# Revit family: 252500.06 OSID Sender høy effekt Vegg
name_source: partatom
category: Fire Alarm Devices
revit_build: Autodesk Revit 2016 (Build: 20160314_0715(x64)
units: mm (PartAtom-declared; Revit-internal decimal feet)

## family parameters
Always vertical = Yes
Cut with Voids When Loaded = No
Maintain Annotation Orientation = No
OmniClass Number = 23.85.30.21.11.11.11
OmniClass Title = Smoke Detectors
Part Type = Normal
Room Calculation Point = No
Round Connector Dimension = Use Diameter
Shared = No
Work Plane-Based = No

## types (1)
- Linjedetektor sender
    Assembly Code = 5423
    CQ 2D Synlig = Yes
    CQ 3D Synlig = No
    CQ Coverage Circle = No
    CQ Coverage Circle Radius = 70000 mm  [stored 229.659 ft]
    CQ Height = 94 mm  [stored 0.308399 ft]
    CQ Høyre = No
    CQ Length = 198 mm  [stored 0.649606 ft]
    CQ Material = <By Category>
    CQ Type = LD
    CQ Type tekst synlig = Yes
    CQ Venstre = Yes
    CQ Width = 130 mm  [stored 0.426509 ft]
    CQFontSymboler = w
    H1 = 55 mm  [stored 0.180446 ft]
    Keynote = XN3
    Manufacturer = Honeywell
    NS8360 = 5423_XN3
    NVMottaker = No
    R = 65 mm  [stored 0.213255 ft]
    Type Comments = -RY

note: [stored X ft] marks values corroborated as IEEE doubles in the binary element streams (Revit-internal decimal feet)

## geometry (parser evidence)
native form markers: Sweep x6
no freeform markers — native parametric forms only
